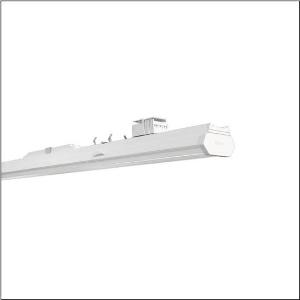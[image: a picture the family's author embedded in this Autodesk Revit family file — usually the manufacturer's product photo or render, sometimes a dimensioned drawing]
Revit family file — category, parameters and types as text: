
# Revit family: licross_r__21_protected_mo_52tp11dn48xg_4e19
name_source: partatom
category: Lighting Fixtures
units: mm (PartAtom-declared; Revit-internal decimal feet)

## family parameters
Cut with Voids When Loaded = No
Host = Face
Light Source = No
Part Type = Normal
Room Calculation Point = No
Round Connector Dimension = Use Diameter
Shared = No

## types (1)
- --- (1 x LED, 8000 lm, 45.5 W, 4000K)
    Apparent Load = 46 VA
    CIE Flux Codes = 83 94 98 100 100
    Color Rendering = 80
    Color Temperature = 4000K
    Default Elevation = 1800 mm
    Description = Licross® 21 Protected MO, luminaire insert, of sheet steel, galvanised, coil coated, white, length: 1.500mm, width: 90mm, height: 103mm, LED rated luminous flux: 8.000lm, light colour: 840, SDCM (Standard Deviation of Colour Matching)MacAdam ≤ 3 SDCM (initial), control gear: DALI 2, with plug, 5-pole, with phase selection, mains connection: 220..240V, AC, 50/60Hz, rated input power: 46W, internal wiring halogen-free, primary light control with lens, of plastic, primary optical cover: cover, of PMMA, light emission: direct distribution, primary light characteristic: symmetric, protection rating (complete): IP64, insulation class (complete): insulation class I (protective earthing), certification: CE, ENEC, VDE, UKCA, protection symbol: D if used in an environment with conductive dust loads with corresponding accessories, impact resistance: IK06, permissible ambient temperature for indoor applications: -25..+45°C, corresponds to IFS (International Featured Standards) requirements for safety and quality in the food industry, reducing of maximum allowable ambient temperature of 5°C with ceiling mounting, LABS conformity tested according to VDMA 24364:2018-05, packaging unit: 1 piece
    Height = 92 mm
    Lamp = 1 x LED
    Lamp Light Flux = 8000 lm
    Lamp Power = 45.5 W
    Lamp count = 1
    Length = 1500 mm
    Luminous efficacy = 176 lm/W
    Manufacturer = Siteco
    ModVariant = No
    Model = 52TP11DN48XG
    Mounting Place = Ceiling
    Mounting Type = Pendant
    Number of Poles = 1
    OnlyDefault = Yes
    Power Factor = 1
    Product Name = Licross® 21 Protected MO
    Product group = luminaire insert | ceiling pendant
    ProductGroupID = 901
    Protection Class = Protection class I
    Protection Degree = IP 64
    RLX_Detail_Level = 1
    RLX_Emergency_Light_Flux = 0 lm
    RLX_Emergency_Type = 0
    RLX_Emergency_Type_DB = No
    RlxData = <blob elided: 24161 chars, md5=245eacb6>
    Socket = socket
    Standby Power = 0 W
    System Light Flux = 8000 lm
    System Power = 46 W
    Type Comments = factory setting: luminous flux: 100 % | dim-lin: 254 | 307 mA
    Type Image = l_1256148.jpg
    URL = http://relux.com
    VarID = @adj_132123
    Voltage = 0 V
    Weight = 0.00 kg
    Width = 88 mm

## geometry (parser evidence)
native form markers: Blend x4, Sweep x12
no freeform markers — native parametric forms only
